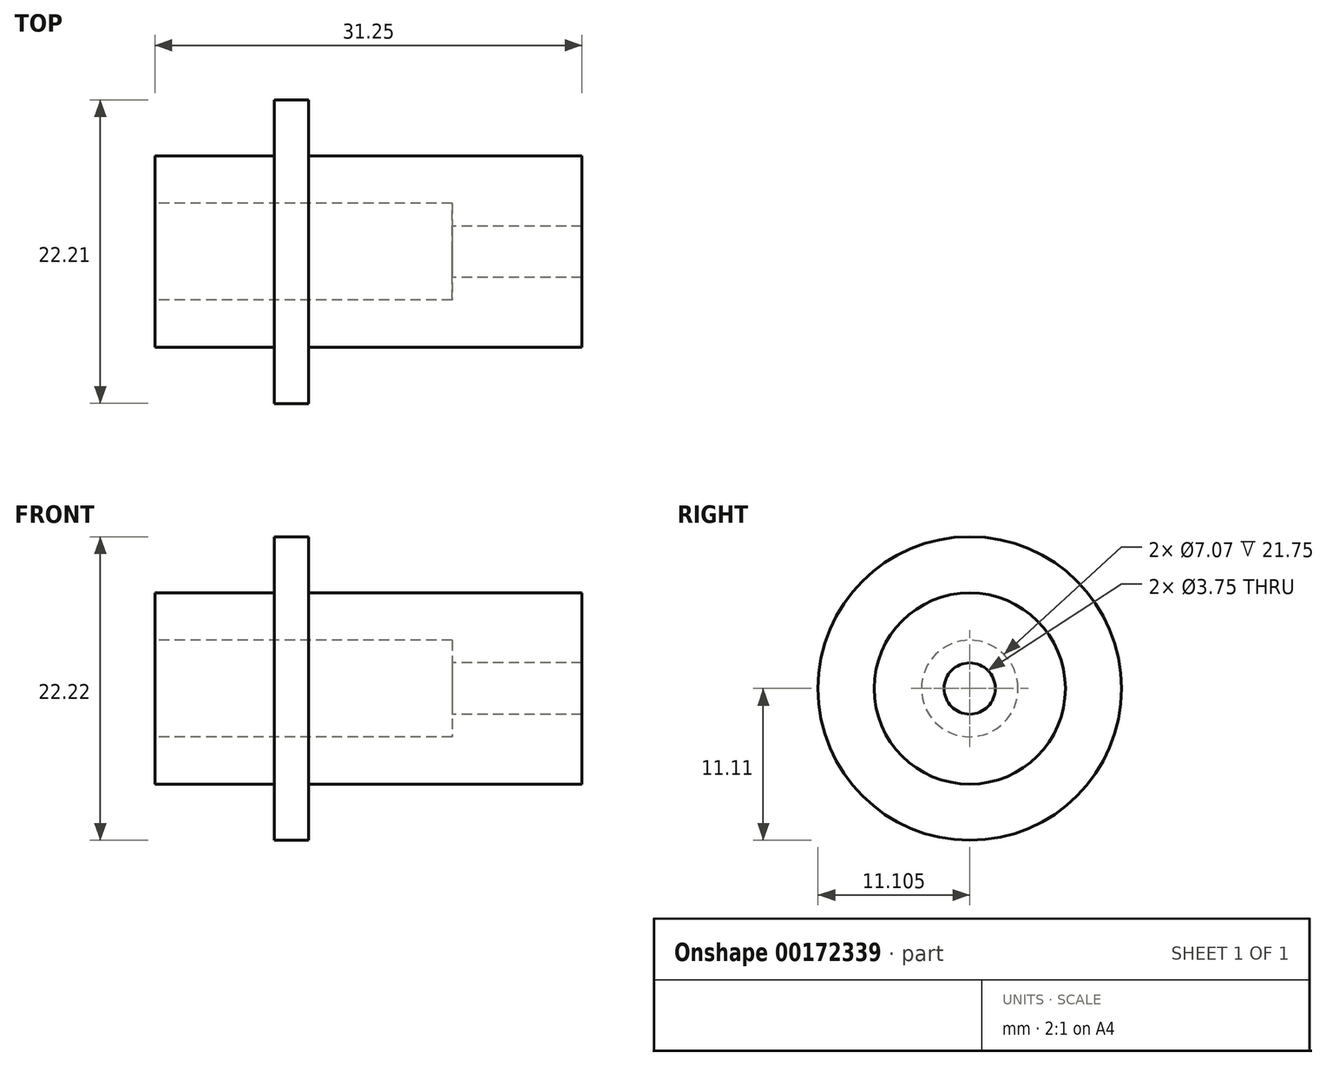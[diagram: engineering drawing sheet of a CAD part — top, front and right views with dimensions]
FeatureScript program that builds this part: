
annotation { "Feature Type Name" : "Feature", "Feature Type Description" : "" }
export const myFeature = defineFeature(function(context is Context, id is Id, definition is map)
    precondition{}
    {
        {
            var Q0;
            Q0=qCreatedBy(makeId("Top.planeOp"),FACE);
            var sketch = newSketch(context, id + "F0", { "sketchPlane" : qUnion([Q0])});
            skLineSegment(sketch, "E0", {"start": v(-8.75, 0) * mm, "end": v(-8.75, 5.12) * mm});
            skLineSegment(sketch, "E1", {"start": v(-8.75, 5.12) * mm, "end": v(0, 5.12) * mm});
            skLineSegment(sketch, "E2", {"start": v(0, 5.12) * mm, "end": v(0, 9.23) * mm});
            skLineSegment(sketch, "E3", {"start": v(0, 9.23) * mm, "end": v(2.5, 9.23) * mm});
            skLineSegment(sketch, "E4", {"start": v(2.5, 9.23) * mm, "end": v(2.5, 5.12) * mm});
            skLineSegment(sketch, "E5", {"start": v(2.5, 5.12) * mm, "end": v(22.5, 5.12) * mm});
            skLineSegment(sketch, "E6", {"start": v(22.5, 5.12) * mm, "end": v(22.5, 0) * mm});
            skPoint(sketch, "E7.orphan", {"position": v(-8.75, 0) * mm});
            skLineSegment(sketch, "E8", {"start": v(-11.44, -1.88) * mm, "end": v(25.78, -1.88) * mm, "construction": true});
            skLineSegment(sketch, "E9", {"start": v(-8.75, 1.66) * mm, "end": v(13, 1.66) * mm});
            skLineSegment(sketch, "E10", {"start": v(13, 1.66) * mm, "end": v(13, 0) * mm});
            skLineSegment(sketch, "E11", {"start": v(13, 0) * mm, "end": v(22.5, 0) * mm});
            skSolve(sketch);
        }
        {
            var Q0;
            Q0 = qSketchRegion(id + "F0", true);
            var Q1;
            Q1=sQuery(id+"F0.wireOp",EDGE,"E8");
            revolve(context, id + "F1", {"entities" : qUnion([Q0]), "axis" : qUnion([Q1]), "revolveType" : RevolveType.FULL});
        }
        {
            var Q0;
            Q0 = qSketchRegion(id + "F0", true);
            var Q1;
            Q1=sQuery(id+"F0.wireOp",EDGE,"E8");
            revolve(context, id + "F2", {"entities" : qUnion([Q0]), "axis" : qUnion([Q1]), "revolveType" : RevolveType.FULL});
        }
    });
